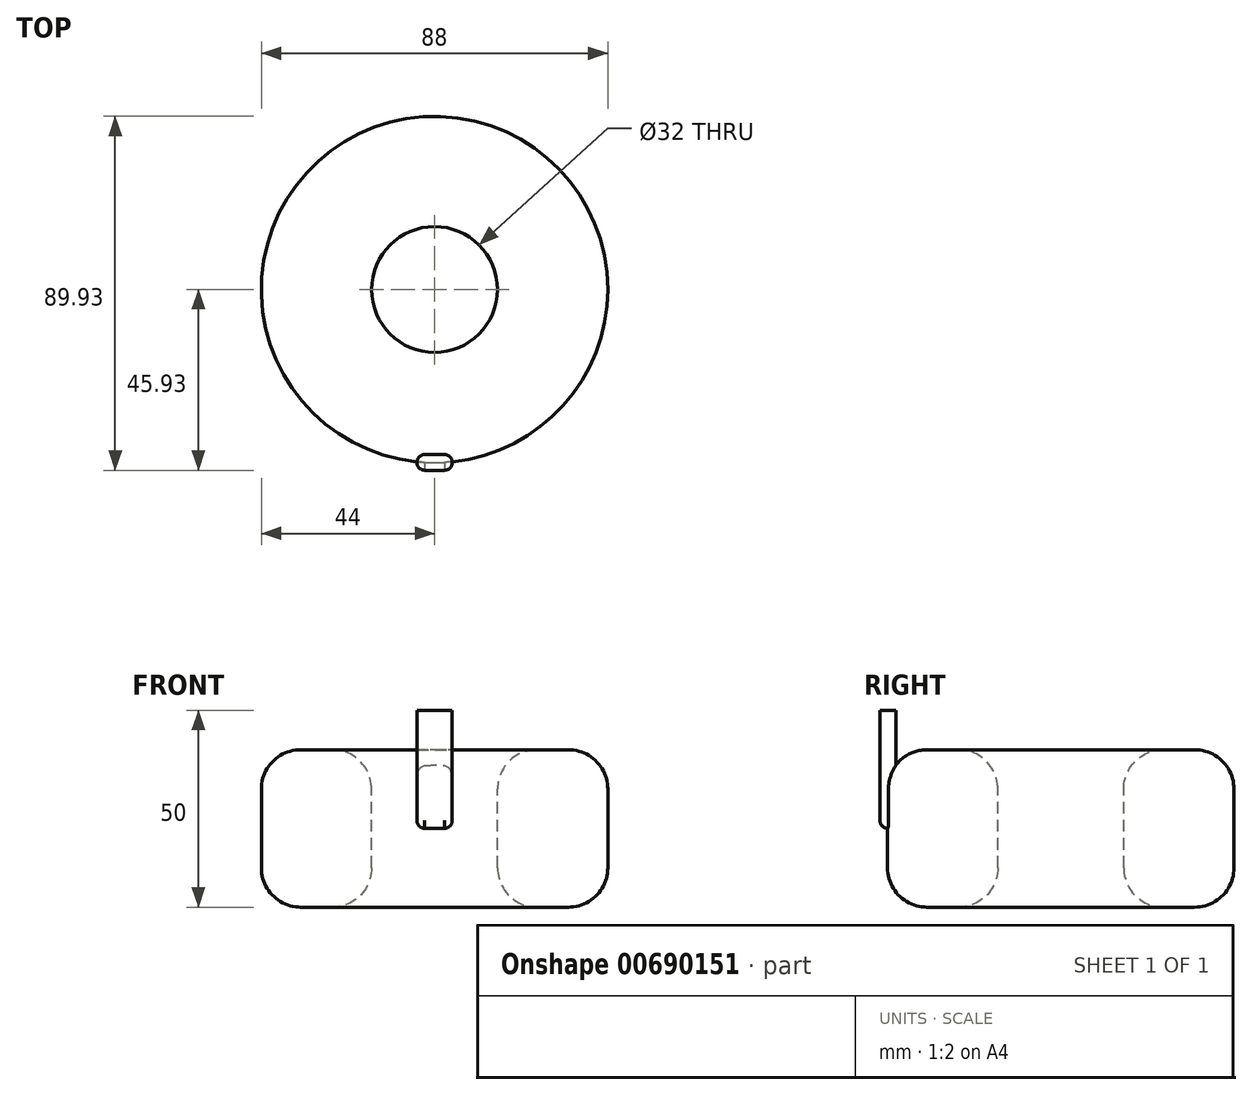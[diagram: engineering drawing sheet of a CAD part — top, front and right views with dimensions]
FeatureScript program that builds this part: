
annotation { "Feature Type Name" : "Feature", "Feature Type Description" : "" }
export const myFeature = defineFeature(function(context is Context, id is Id, definition is map)
    precondition{}
    {
        {
            var Q0;
            Q0=qCreatedBy(makeId("Top.planeOp"),FACE);
            var sketch = newSketch(context, id + "F0", { "sketchPlane" : qUnion([Q0])});
            skCircle(sketch, "E0", {"center": v(0, 0) * mm, "radius": 16 * mm});
            skCircle(sketch, "E1", {"center": v(0, 0) * mm, "radius": 44 * mm});
            skSolve(sketch);
        }
        {
            var Q0;
            Q0 = qSketchRegion(id + "F0", true);
            extrude(context, id + "F1", {"entities" : qUnion([Q0]), "endBound" : BoundingType.SYMMETRIC, "oppositeDirection" : true, "depth" : 40 * mm, "offsetDistance" : 25 * mm});
        }
        {
            var Q0;
            Q0=makeQuery(id+"F1.opExtrude","SWEPT_FACE",FACE,{"disambiguationData":[OSD([sQuery(id+"F0.wireOp",EDGE,"E0")])]});
            var Q1;
            Q1=makeQuery(id+"F1.opExtrude","SWEPT_FACE",FACE,{"disambiguationData":[OSD([sQuery(id+"F0.wireOp",EDGE,"E1")])]});
            fillet(context, id + "F2", {"entities" : qUnion([Q0, Q1]), "tangentPropagation" : true, "radius" : 10 * mm, "defaultsChanged" : false, "vertexSettings" : [], "allowEdgeOverflow" : false});
        }
        {
            var Q0;
            Q0=qCreatedBy(makeId("Top.planeOp"),FACE);
            var sketch = newSketch(context, id + "F3", { "sketchPlane" : qUnion([Q0])});
            skArc(sketch, "E2", {"start": v(-2.5, -41.93) * mm, "mid": v(-4.5, -43.93) * mm, "end": v(-2.5, -45.93) * mm});
            skLineSegment(sketch, "E3", {"start": v(2.5, -41.93) * mm, "end": v(-2.5, -41.93) * mm});
            skLineSegment(sketch, "E4", {"start": v(-2.5, -45.93) * mm, "end": v(2.5, -45.93) * mm});
            skArc(sketch, "E5.trimOffspring", {"start": v(2.5, -41.93) * mm, "mid": v(4.5, -43.93) * mm, "end": v(2.5, -45.93) * mm});
            skSolve(sketch);
        }
        {
            var Q0;
            Q0 = qSketchRegion(id + "F3", true);
            extrude(context, id + "F4", {"entities" : qUnion([Q0]), "operationType" : NewBodyOperationType.ADD, "depth" : 30 * mm, "offsetDistance" : 25 * mm});
        }
        {
            var Q0;
            Q0=makeQuery(id+"F4.opExtrude","CAP_EDGE",EDGE,{"disambiguationData":[OSD([sQuery(id+"F3.wireOp",EDGE,"E4")])],"isStart":true});
            fillet(context, id + "F5", {"entities" : qUnion([Q0]), "tangentPropagation" : true, "radius" : 2 * mm, "defaultsChanged" : true, "vertexSettings" : [], "allowEdgeOverflow" : false});
        }
    });
